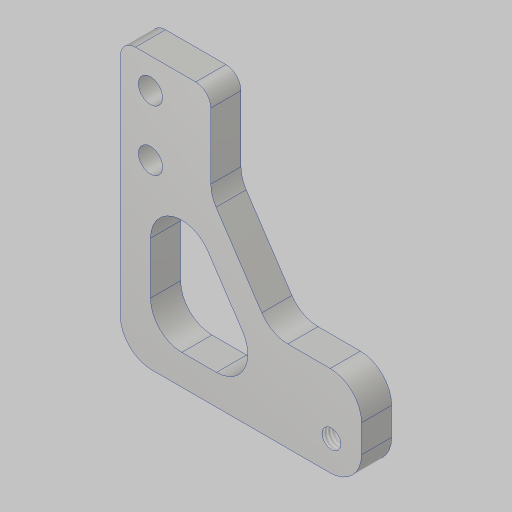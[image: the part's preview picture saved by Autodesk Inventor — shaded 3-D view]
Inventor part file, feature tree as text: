
AUTODESK INVENTOR PART (.ipt)
format: ipt  version: 2023.5 (Build 275446000, 446)  size: 166,912 bytes
history: native  units: in
note: dims shown in document units (in); Inventor stores cm internally (conversion verified against a paired STEP export)
features: hole x2, fillet x2, sketch x1, extrude x1
ambient origin geometry x8: Origin, YZ Plane, XZ Plane, XY Plane, X Axis, Y Axis, Z Axis, Center Point
bodies: Solid1 (feature_tree)
feature tree (6):
  sketch  "Sketch1"  dims[d0=0.75in d1=1.5in d2=0.5in d4=0.25in d5=0.25in d6=0.0in d7=0.201in d8=0.75in d9=0.375in d10=0.19in d11=0.5635in d12=1.0in d13=0.8108in d14=0.156in d15=0.38in d16=0.375in d17=0.25in d18=0.5635in d19=1.0in d20=0.8108in d21=0.125in d22=1.25in d24=0.75in d26=0.75in d27=0.25in d28=0.25in d29=0.201in d30=0.25in d31=0.25in d32=0.26in d33=2.0in d35=0.25in d36=1.5in]
  extrude  "Extrusion1"  Depth=1.5in
  hole  "Hole1"  [1 undecoded]
  hole  "Hole2"  [1 undecoded]
  fillet  "Fillet1"  Radius=0.25in
  fillet  "Fillet2"  Radius=0.125in
note: 2 required parameter values undecoded (feature->parameter linkage not recoverable at this tier; creation-order binding heuristic only, values carry confidence <= 0.55)
